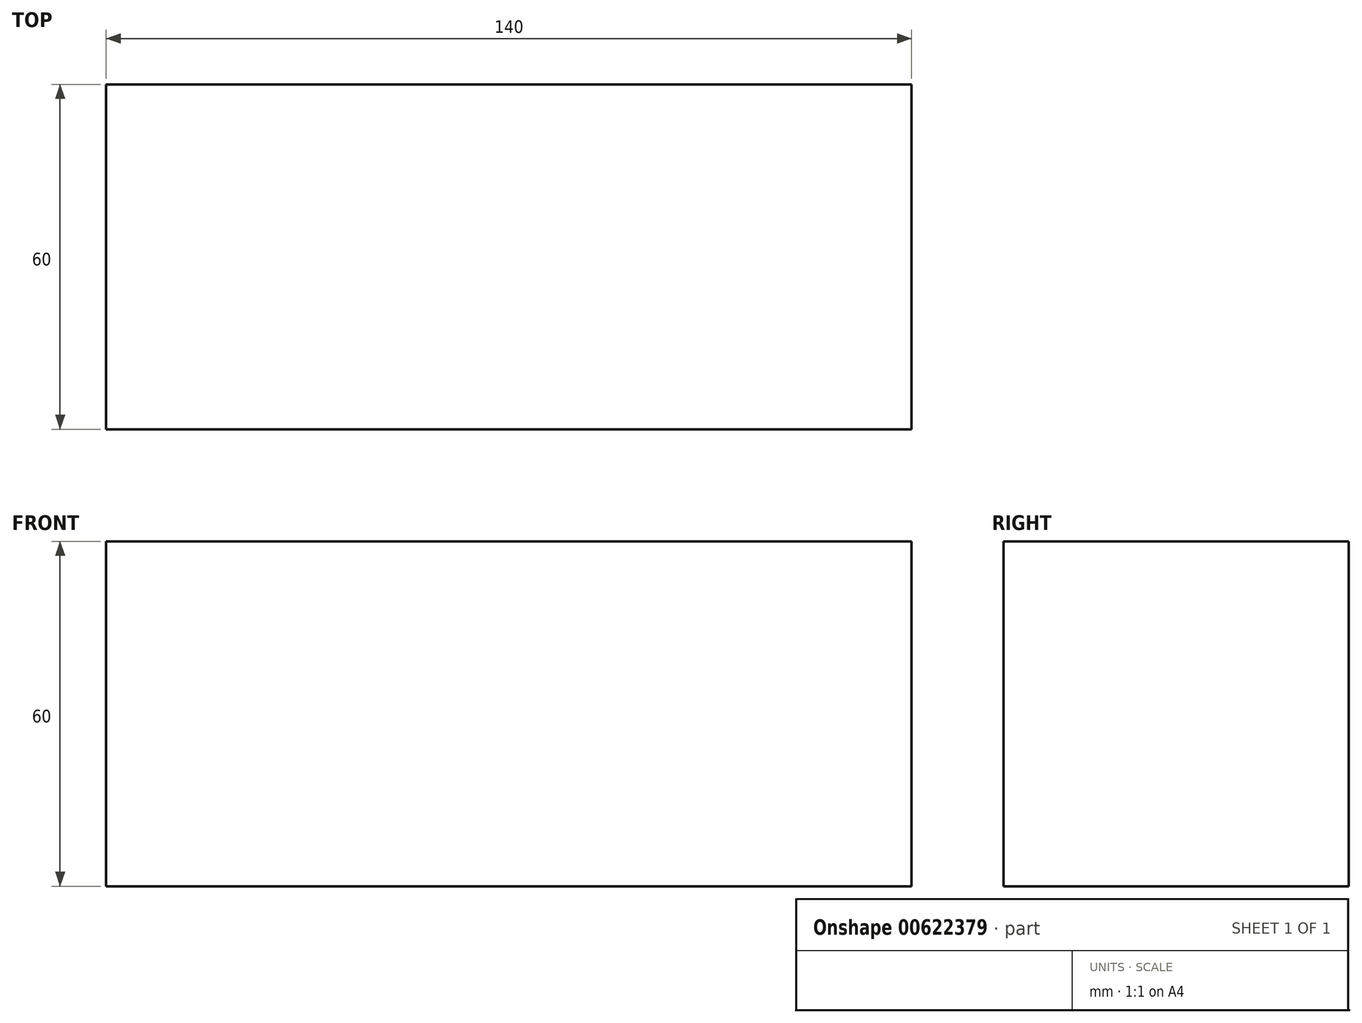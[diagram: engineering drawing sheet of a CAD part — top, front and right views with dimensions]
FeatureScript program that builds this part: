
annotation { "Feature Type Name" : "Feature", "Feature Type Description" : "" }
export const myFeature = defineFeature(function(context is Context, id is Id, definition is map)
    precondition{}
    {
        {
            var Q0;
            Q0=qCreatedBy(makeId("Top.planeOp"),FACE);
            var sketch = newSketch(context, id + "F0", { "sketchPlane" : qUnion([Q0])});
            skLineSegment(sketch, "E0.bottom", {"start": v(-70, 30) * mm, "end": v(70, 30) * mm});
            skLineSegment(sketch, "E0.top", {"start": v(-70, -30) * mm, "end": v(70, -30) * mm});
            skLineSegment(sketch, "E0.left", {"start": v(-70, 30) * mm, "end": v(-70, -30) * mm});
            skLineSegment(sketch, "E0.right", {"start": v(70, 30) * mm, "end": v(70, -30) * mm});
            skPoint(sketch, "E0.middle", {"position": v(0, 0) * mm});
            skSolve(sketch);
        }
        {
            var Q0;
            Q0=makeQuery(id+"F0.imprint","IMPRINT",FACE,{"disambiguationData":[TD([[makeQuery(id+"F0.imprint","IMPRINT",EDGE,{"derivedFrom":sQuery(id+"F0.wireOp",EDGE,"E0.bottom")}),-1.0]])]});
            extrude(context, id + "F1", {"entities" : qUnion([Q0]), "depth" : 60 * mm, "offsetDistance" : 25 * mm});
        }
        {
            var Q0;
            Q0=makeQuery(id+"F1.opExtrude","CAP_FACE",FACE,{"disambiguationData":[OSD([sQuery(id+"F0.wireOp",EDGE,"E0.bottom"),sQuery(id+"F0.wireOp",EDGE,"E0.top"),sQuery(id+"F0.wireOp",EDGE,"E0.left"),sQuery(id+"F0.wireOp",EDGE,"E0.right")])],"isStart":false});
            var sketch = newSketch(context, id + "F2", { "sketchPlane" : qUnion([Q0])});
            skCircle(sketch, "E1", {"center": v(0, 0) * mm, "radius": 10 * mm});
            skSolve(sketch);
        }
        {
            var Q0;
            Q0=makeQuery(id+"F2.imprint","IMPRINT",FACE,{"disambiguationData":[TD([[makeQuery(id+"F2.imprint","IMPRINT",EDGE,{"derivedFrom":sQuery(id+"F2.wireOp",EDGE,"E1")}),1.0]])]});
            var sketch = newSketch(context, id + "F3", { "sketchPlane" : qUnion([Q0])});
            skCircle(sketch, "E2", {"center": v(40, 0) * mm, "radius": 10 * mm});
            skCircle(sketch, "E3", {"center": v(-40, 0) * mm, "radius": 10 * mm});
            skSolve(sketch);
        }
        {
            var Q0;
            Q0=sQuery(id+"F3.wireOp",EDGE,"E3");
            extrude(context, id + "F4", {"bodyType" : ToolBodyType.SURFACE, "surfaceEntities" : qUnion([Q0]), "oppositeDirection" : true, "depth" : 25 * mm, "offsetDistance" : 25 * mm});
        }
        {
            var Q0;
            Q0=sQuery(id+"F3.wireOp",EDGE,"E3");
            extrude(context, id + "F5", {"bodyType" : ToolBodyType.SURFACE, "surfaceEntities" : qUnion([Q0]), "depth" : 25 * mm, "offsetDistance" : 25 * mm});
        }
        {
            var Q0;
            Q0=sQuery(id+"F2.wireOp",EDGE,"E1");
            extrude(context, id + "F6", {"bodyType" : ToolBodyType.SURFACE, "surfaceEntities" : qUnion([Q0]), "oppositeDirection" : true, "depth" : 10 * mm, "offsetDistance" : 25 * mm});
        }
        {
            var Q0;
            Q0=sQuery(id+"F3.wireOp",EDGE,"E2");
            extrude(context, id + "F7", {"bodyType" : ToolBodyType.SURFACE, "surfaceEntities" : qUnion([Q0]), "depth" : 10 * mm, "offsetDistance" : 25 * mm});
        }
    });
